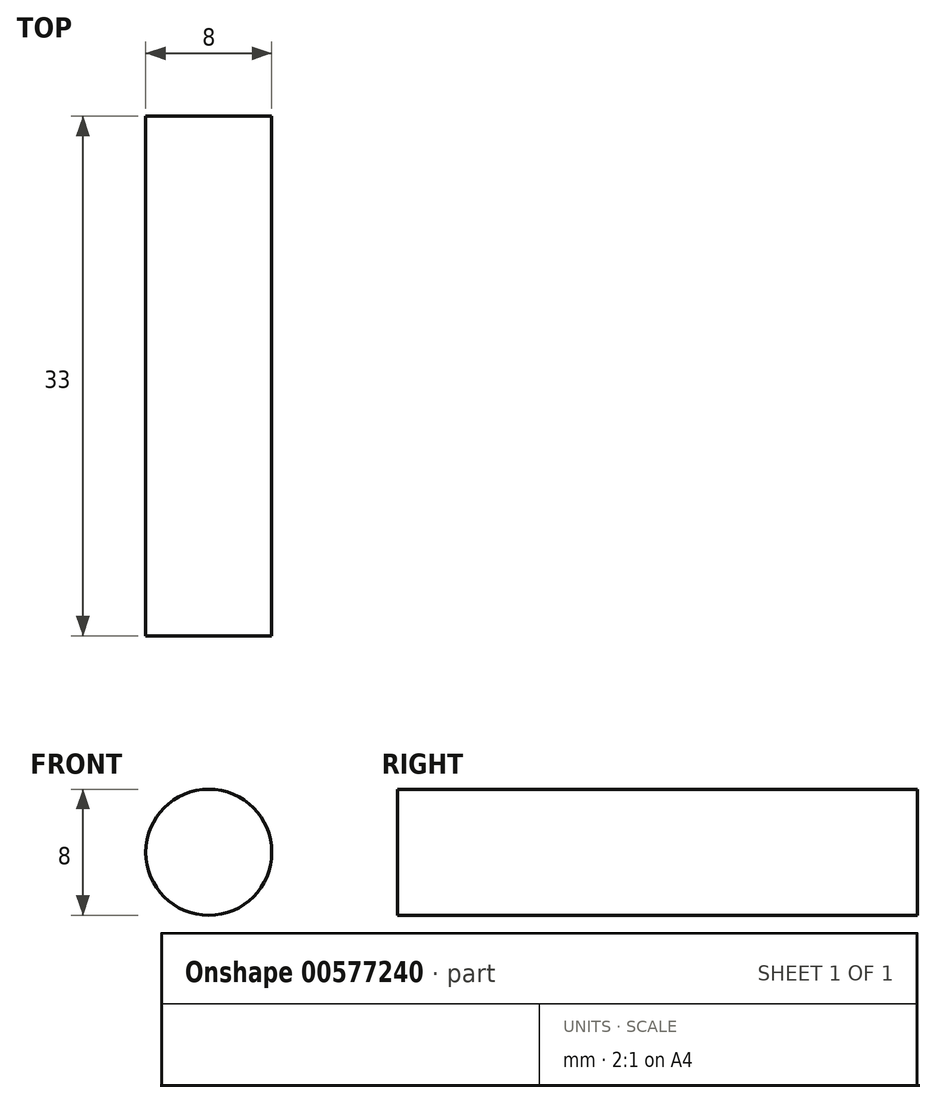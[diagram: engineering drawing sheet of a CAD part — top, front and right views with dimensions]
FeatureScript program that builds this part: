
annotation { "Feature Type Name" : "Feature", "Feature Type Description" : "" }
export const myFeature = defineFeature(function(context is Context, id is Id, definition is map)
    precondition{}
    {
        {
            var Q0;
            Q0=qCreatedBy(makeId("Front.planeOp"),FACE);
            var sketch = newSketch(context, id + "F0", { "sketchPlane" : qUnion([Q0])});
            skCircle(sketch, "E0", {"center": v(0, 0) * mm, "radius": 4 * mm});
            skSolve(sketch);
        }
        {
            var Q0;
            Q0 = qSketchRegion(id + "F0", true);
            extrude(context, id + "F1", {"entities" : qUnion([Q0]), "depth" : 33 * mm, "offsetDistance" : 25 * mm});
        }
    });
